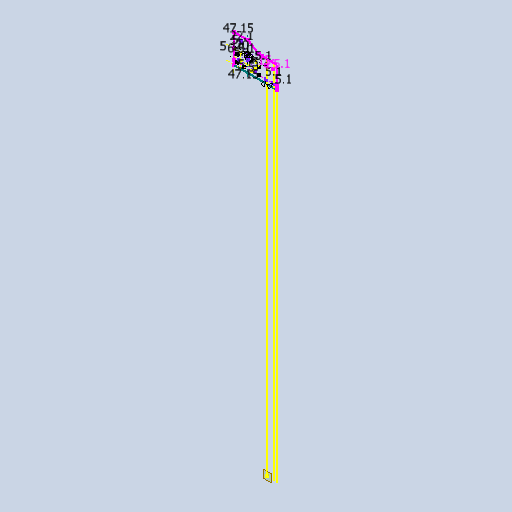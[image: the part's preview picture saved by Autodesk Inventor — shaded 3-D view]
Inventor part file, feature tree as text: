
AUTODESK INVENTOR PART (.ipt)
format: ipt  version: 2023.2 (Build 272271000, 271)  size: 201,216 bytes
history: native  units: mm
features: reference x25, other x4, plane x2, sketch x1
ambient origin geometry x8: Origin, YZ Plane, XZ Plane, XY Plane, X Axis, Y Axis, Z Axis, Center Point
feature tree (32):
  plane  "Work Plane1"
  sketch  "Sketch1"  dims[d0=5.1mm d2=5.1mm d9=5.1mm d10=15.0mm d11=15.0mm d17=47.15mm d22=5.0mm d23=5.0mm d24=5.0mm d29=20.0mm d30=6.0mm d31=47.15mm d32=22.1mm d33=5.1mm d34=5.1mm d35=5.1mm d36=5.1mm d37=5.1mm]
  plane  "Work Plane2"
  reference  "Reference1"
  reference  "Reference2"
  reference  "Reference3"
  reference  "Reference4"
  reference  "Reference5"
  reference  "Reference6"
  reference  "Reference7"
  reference  "Reference8"
  reference  "Reference9"
  reference  "Reference10"
  reference  "Reference11"
  reference  "Reference12"
  reference  "Reference13"
  reference  "Reference14"
  reference  "Reference15"
  reference  "Reference16"
  reference  "Reference17"
  reference  "Reference18"
  reference  "Reference19"
  reference  "Reference20"
  reference  "Reference21"
  reference  "Reference22"
  reference  "Reference23"
  reference  "Reference24"
  reference  "Reference25"
  parser-record x1  (decoder bookkeeping rows leaked as tree rows — omitted from the tree; the rows remain in map.json)
  other  "Main Assembly.iam"
  other  "C beam extrusion 250:2"
  other  "20x40 1000:1"
note: 1 file-system path scrubbed to <path> (originals preserved in map.json)
